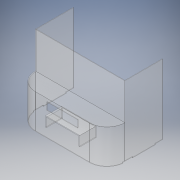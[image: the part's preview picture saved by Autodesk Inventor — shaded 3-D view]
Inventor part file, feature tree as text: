
AUTODESK INVENTOR PART (.ipt)
format: ipt  version: 2018 (Build 220112000, 112)  size: 218,112 bytes
history: native  units: in
note: dims shown in document units (in); Inventor stores cm internally (conversion verified against a paired STEP export)
features: extrude x4, sketch x4, imported_body x1
ambient origin geometry x8: Origin, YZ Plane, XZ Plane, XY Plane, X Axis, Y Axis, Z Axis, Center Point
bodies: Solid1 (feature_tree)
feature tree (9):
  extrude  "Extrusion1"  Depth=7.4803in TaperAngle=0.0deg
  extrude  "Extrusion2"  Depth=2.1496in
  extrude  "Extrusion3"  Depth=0.1181in TaperAngle=0.0deg
  extrude  "Extrusion4"  [1 undecoded]
  sketch  "Sketch1"  dims[d0=3.7795in d1=7.4803in d2=0.0in]
  sketch  "Sketch2"  dims[d3=7.4803in d4=0.0in d7=2.1496in]
  sketch  "Sketch3"  dims[d8=0.1969in d9=0.0in d10=0.1181in d11=0.0in]
  sketch  "Sketch4"
  imported_body  "Imported1"
note: 1 required parameter value undecoded (feature->parameter linkage not recoverable at this tier; creation-order binding heuristic only, values carry confidence <= 0.55)
